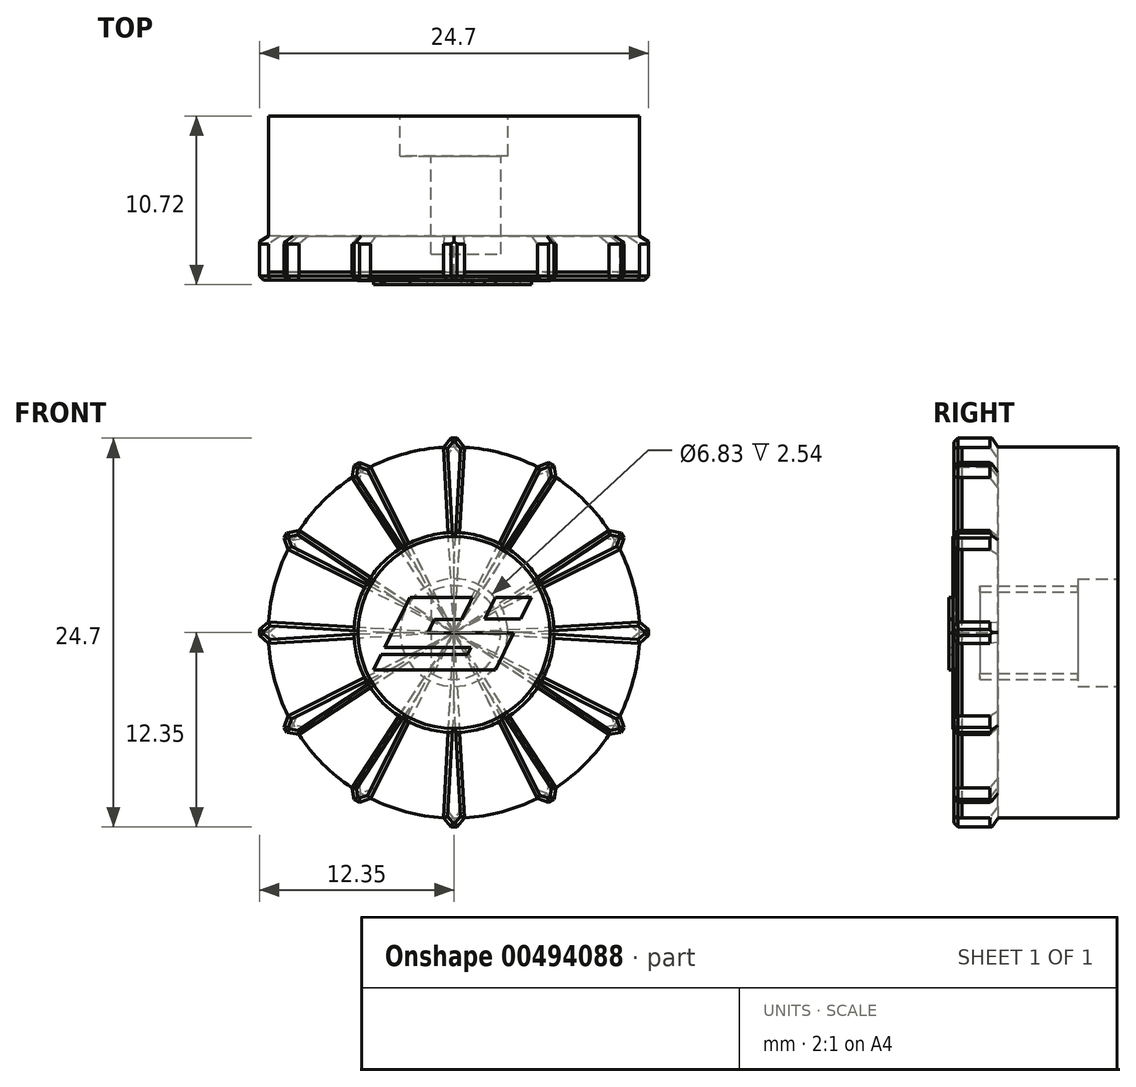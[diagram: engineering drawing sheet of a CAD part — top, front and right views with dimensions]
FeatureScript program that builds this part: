
annotation { "Feature Type Name" : "Feature", "Feature Type Description" : "" }
export const myFeature = defineFeature(function(context is Context, id is Id, definition is map)
    precondition{}
    {
        {
            var Q0;
            Q0=qCreatedBy(makeId("Front.planeOp"),FACE);
            var sketch = newSketch(context, id + "F0", { "sketchPlane" : qUnion([Q0])});
            skCircle(sketch, "E0", {"center": v(-36.3, 18.86) * mm, "radius": 11.79 * mm});
            skSolve(sketch);
        }
        {
            var Q0;
            Q0=makeQuery(id+"F0.imprint","IMPRINT",FACE,{"disambiguationData":[TD([[makeQuery(id+"F0.imprint","IMPRINT",EDGE,{"derivedFrom":sQuery(id+"F0.wireOp",EDGE,"E0")}),1.0]])]});
            extrude(context, id + "F1", {"entities" : qUnion([Q0]), "depth" : 9.9 * mm});
        }
        {
            var Q0;
            Q0=makeQuery(id+"F1.opExtrude","CAP_FACE",FACE,{"disambiguationData":[OSD([sQuery(id+"F0.wireOp",EDGE,"E0")])],"isStart":true});
            var sketch = newSketch(context, id + "F2", { "sketchPlane" : qUnion([Q0])});
            skArc(sketch, "E1", {"start": v(37.76, 21.44) * mm, "mid": v(33.32, 18.86) * mm, "end": v(37.76, 16.28) * mm});
            skLineSegment(sketch, "E2", {"start": v(37.76, 21.44) * mm, "end": v(37.76, 16.28) * mm});
            skSolve(sketch);
        }
        {
            var Q0;
            Q0=makeQuery(id+"F2.imprint","IMPRINT",FACE,{"disambiguationData":[TD([[makeQuery(id+"F2.imprint","IMPRINT",EDGE,{"derivedFrom":sQuery(id+"F2.wireOp",EDGE,"E1")}),1.0]])]});
            extrude(context, id + "F3", {"entities" : qUnion([Q0]), "operationType" : NewBodyOperationType.REMOVE, "oppositeDirection" : true, "depth" : 8.76 * mm});
        }
        {
            var Q0;
            Q0=makeQuery(id+"F1.opExtrude","CAP_FACE",FACE,{"disambiguationData":[OSD([sQuery(id+"F0.wireOp",EDGE,"E0")])],"isStart":true});
            var sketch = newSketch(context, id + "F4", { "sketchPlane" : qUnion([Q0])});
            skCircle(sketch, "E3", {"center": v(36.3, 18.86) * mm, "radius": 3.42 * mm});
            skSolve(sketch);
        }
        {
            var Q0;
            Q0=makeQuery(id+"F4.imprint","IMPRINT",FACE,{"disambiguationData":[TD([[makeQuery(id+"F4.imprint","IMPRINT",EDGE,{"derivedFrom":sQuery(id+"F4.wireOp",EDGE,"E3")}),1.0]])]});
            var Q1;
            Q1=sQuery(id+"F4.wireOp",EDGE,"E3");
            extrude(context, id + "F5", {"entities" : qUnion([Q0]), "operationType" : NewBodyOperationType.REMOVE, "surfaceEntities" : qUnion([Q1]), "oppositeDirection" : true, "depth" : 2.54 * mm});
        }
        {
            var Q0;
            Q0=qCreatedBy(makeId("Front.planeOp"),FACE);
            var sketch = newSketch(context, id + "F6", { "sketchPlane" : qUnion([Q0])});
            skLineSegment(sketch, "E4", {"start": v(-36.97, 30.63) * mm, "end": v(-36.48, 31.2) * mm});
            skLineSegment(sketch, "E5", {"start": v(-36.48, 31.2) * mm, "end": v(-36.1, 31.2) * mm});
            skLineSegment(sketch, "E6", {"start": v(-36.1, 31.2) * mm, "end": v(-35.6, 30.63) * mm});
            skLineSegment(sketch, "E7", {"start": v(-36.3, 18.86) * mm, "end": v(-36.97, 30.63) * mm});
            skLineSegment(sketch, "E8", {"start": v(-35.6, 30.63) * mm, "end": v(-36.3, 18.86) * mm});
            skLineSegment(sketch, "E9.1.0", {"start": v(-41.58, 29.39) * mm, "end": v(-36.3, 18.86) * mm});
            skLineSegment(sketch, "E9.1.1", {"start": v(-36.3, 18.86) * mm, "end": v(-42.76, 28.7) * mm});
            skLineSegment(sketch, "E9.1.2", {"start": v(-42.76, 28.7) * mm, "end": v(-42.63, 29.46) * mm});
            skLineSegment(sketch, "E9.1.3", {"start": v(-42.63, 29.46) * mm, "end": v(-42.3, 29.65) * mm});
            skLineSegment(sketch, "E9.1.4", {"start": v(-42.3, 29.65) * mm, "end": v(-41.58, 29.39) * mm});
            skLineSegment(sketch, "E9.2.0", {"start": v(-46.14, 25.33) * mm, "end": v(-36.3, 18.86) * mm});
            skLineSegment(sketch, "E9.2.1", {"start": v(-36.3, 18.86) * mm, "end": v(-46.82, 24.15) * mm});
            skLineSegment(sketch, "E9.2.2", {"start": v(-46.82, 24.15) * mm, "end": v(-47.08, 24.87) * mm});
            skLineSegment(sketch, "E9.2.3", {"start": v(-47.08, 24.87) * mm, "end": v(-46.9, 25.2) * mm});
            skLineSegment(sketch, "E9.2.4", {"start": v(-46.9, 25.2) * mm, "end": v(-46.14, 25.33) * mm});
            skLineSegment(sketch, "E9.3.0", {"start": v(-48.06, 19.54) * mm, "end": v(-36.3, 18.86) * mm});
            skLineSegment(sketch, "E9.3.1", {"start": v(-36.3, 18.86) * mm, "end": v(-48.06, 18.18) * mm});
            skLineSegment(sketch, "E9.3.2", {"start": v(-48.06, 18.18) * mm, "end": v(-48.64, 18.67) * mm});
            skLineSegment(sketch, "E9.3.3", {"start": v(-48.64, 18.67) * mm, "end": v(-48.64, 19.05) * mm});
            skLineSegment(sketch, "E9.3.4", {"start": v(-48.64, 19.05) * mm, "end": v(-48.06, 19.54) * mm});
            skLineSegment(sketch, "E9.4.0", {"start": v(-46.82, 13.57) * mm, "end": v(-36.3, 18.86) * mm});
            skLineSegment(sketch, "E9.4.1", {"start": v(-36.3, 18.86) * mm, "end": v(-46.14, 12.39) * mm});
            skLineSegment(sketch, "E9.4.2", {"start": v(-46.14, 12.39) * mm, "end": v(-46.9, 12.52) * mm});
            skLineSegment(sketch, "E9.4.3", {"start": v(-46.9, 12.52) * mm, "end": v(-47.08, 12.85) * mm});
            skLineSegment(sketch, "E9.4.4", {"start": v(-47.08, 12.85) * mm, "end": v(-46.82, 13.57) * mm});
            skLineSegment(sketch, "E9.5.0", {"start": v(-42.76, 9.01) * mm, "end": v(-36.3, 18.86) * mm});
            skLineSegment(sketch, "E9.5.1", {"start": v(-36.3, 18.86) * mm, "end": v(-41.58, 8.33) * mm});
            skLineSegment(sketch, "E9.5.2", {"start": v(-41.58, 8.33) * mm, "end": v(-42.3, 8.07) * mm});
            skLineSegment(sketch, "E9.5.3", {"start": v(-42.3, 8.07) * mm, "end": v(-42.63, 8.26) * mm});
            skLineSegment(sketch, "E9.5.4", {"start": v(-42.63, 8.26) * mm, "end": v(-42.76, 9.01) * mm});
            skLineSegment(sketch, "E9.6.0", {"start": v(-36.97, 7.1) * mm, "end": v(-36.3, 18.86) * mm});
            skLineSegment(sketch, "E9.6.1", {"start": v(-36.3, 18.86) * mm, "end": v(-35.6, 7.1) * mm});
            skLineSegment(sketch, "E9.6.2", {"start": v(-35.6, 7.1) * mm, "end": v(-36.1, 6.5) * mm});
            skLineSegment(sketch, "E9.6.3", {"start": v(-36.1, 6.5) * mm, "end": v(-36.48, 6.5) * mm});
            skLineSegment(sketch, "E9.6.4", {"start": v(-36.48, 6.5) * mm, "end": v(-36.97, 7.1) * mm});
            skLineSegment(sketch, "E9.7.0", {"start": v(-31, 8.33) * mm, "end": v(-36.3, 18.86) * mm});
            skLineSegment(sketch, "E9.7.1", {"start": v(-36.3, 18.86) * mm, "end": v(-29.82, 9.01) * mm});
            skLineSegment(sketch, "E9.7.2", {"start": v(-29.82, 9.01) * mm, "end": v(-29.95, 8.26) * mm});
            skLineSegment(sketch, "E9.7.3", {"start": v(-29.95, 8.26) * mm, "end": v(-30.28, 8.07) * mm});
            skLineSegment(sketch, "E9.7.4", {"start": v(-30.28, 8.07) * mm, "end": v(-31, 8.33) * mm});
            skLineSegment(sketch, "E9.8.0", {"start": v(-26.44, 12.39) * mm, "end": v(-36.3, 18.86) * mm});
            skLineSegment(sketch, "E9.8.1", {"start": v(-36.3, 18.86) * mm, "end": v(-25.76, 13.57) * mm});
            skLineSegment(sketch, "E9.8.2", {"start": v(-25.76, 13.57) * mm, "end": v(-25.5, 12.85) * mm});
            skLineSegment(sketch, "E9.8.3", {"start": v(-25.5, 12.85) * mm, "end": v(-25.7, 12.52) * mm});
            skLineSegment(sketch, "E9.8.4", {"start": v(-25.7, 12.52) * mm, "end": v(-26.44, 12.39) * mm});
            skLineSegment(sketch, "E9.9.0", {"start": v(-24.52, 18.18) * mm, "end": v(-36.3, 18.86) * mm});
            skLineSegment(sketch, "E9.9.1", {"start": v(-36.3, 18.86) * mm, "end": v(-24.52, 19.54) * mm});
            skLineSegment(sketch, "E9.9.2", {"start": v(-24.52, 19.54) * mm, "end": v(-23.94, 19.05) * mm});
            skLineSegment(sketch, "E9.9.3", {"start": v(-23.94, 19.05) * mm, "end": v(-23.94, 18.67) * mm});
            skLineSegment(sketch, "E9.9.4", {"start": v(-23.94, 18.67) * mm, "end": v(-24.52, 18.18) * mm});
            skLineSegment(sketch, "E9.10.0", {"start": v(-25.76, 24.15) * mm, "end": v(-36.3, 18.86) * mm});
            skLineSegment(sketch, "E9.10.1", {"start": v(-36.3, 18.86) * mm, "end": v(-26.44, 25.33) * mm});
            skLineSegment(sketch, "E9.10.2", {"start": v(-26.44, 25.33) * mm, "end": v(-25.7, 25.2) * mm});
            skLineSegment(sketch, "E9.10.3", {"start": v(-25.7, 25.2) * mm, "end": v(-25.5, 24.87) * mm});
            skLineSegment(sketch, "E9.10.4", {"start": v(-25.5, 24.87) * mm, "end": v(-25.76, 24.15) * mm});
            skLineSegment(sketch, "E9.11.0", {"start": v(-29.82, 28.7) * mm, "end": v(-36.3, 18.86) * mm});
            skLineSegment(sketch, "E9.11.1", {"start": v(-36.3, 18.86) * mm, "end": v(-31, 29.39) * mm});
            skLineSegment(sketch, "E9.11.2", {"start": v(-31, 29.39) * mm, "end": v(-30.28, 29.65) * mm});
            skLineSegment(sketch, "E9.11.3", {"start": v(-30.28, 29.65) * mm, "end": v(-29.95, 29.46) * mm});
            skLineSegment(sketch, "E9.11.4", {"start": v(-29.95, 29.46) * mm, "end": v(-29.82, 28.7) * mm});
            skPoint(sketch, "E9.center", {"position": v(-36.3, 18.86) * mm});
            skSolve(sketch);
        }
        {
            var Q0;
            Q0=makeQuery(id+"F6.imprint","IMPRINT",FACE,{"disambiguationData":[TD([[makeQuery(id+"F6.imprint","IMPRINT",EDGE,{"derivedFrom":sQuery(id+"F6.wireOp",EDGE,"E9.8.0")}),-1.0]])]});
            var Q1;
            Q1=makeQuery(id+"F6.imprint","IMPRINT",FACE,{"disambiguationData":[TD([[makeQuery(id+"F6.imprint","IMPRINT",EDGE,{"derivedFrom":sQuery(id+"F6.wireOp",EDGE,"E9.9.0")}),-1.0]])]});
            var Q2;
            Q2=makeQuery(id+"F6.imprint","IMPRINT",FACE,{"disambiguationData":[TD([[makeQuery(id+"F6.imprint","IMPRINT",EDGE,{"derivedFrom":sQuery(id+"F6.wireOp",EDGE,"E9.10.0")}),-1.0]])]});
            var Q3;
            Q3=makeQuery(id+"F6.imprint","IMPRINT",FACE,{"disambiguationData":[TD([[makeQuery(id+"F6.imprint","IMPRINT",EDGE,{"derivedFrom":sQuery(id+"F6.wireOp",EDGE,"E9.11.0")}),-1.0]])]});
            var Q4;
            Q4=makeQuery(id+"F6.imprint","IMPRINT",FACE,{"disambiguationData":[TD([[makeQuery(id+"F6.imprint","IMPRINT",EDGE,{"derivedFrom":sQuery(id+"F6.wireOp",EDGE,"E4")}),-1.0]])]});
            var Q5;
            Q5=makeQuery(id+"F6.imprint","IMPRINT",FACE,{"disambiguationData":[TD([[makeQuery(id+"F6.imprint","IMPRINT",EDGE,{"derivedFrom":sQuery(id+"F6.wireOp",EDGE,"E9.2.0")}),-1.0]])]});
            var Q6;
            Q6=makeQuery(id+"F6.imprint","IMPRINT",FACE,{"disambiguationData":[TD([[makeQuery(id+"F6.imprint","IMPRINT",EDGE,{"derivedFrom":sQuery(id+"F6.wireOp",EDGE,"E9.3.0")}),-1.0]])]});
            var Q7;
            Q7=makeQuery(id+"F6.imprint","IMPRINT",FACE,{"disambiguationData":[TD([[makeQuery(id+"F6.imprint","IMPRINT",EDGE,{"derivedFrom":sQuery(id+"F6.wireOp",EDGE,"E9.4.0")}),-1.0]])]});
            var Q8;
            Q8=makeQuery(id+"F6.imprint","IMPRINT",FACE,{"disambiguationData":[TD([[makeQuery(id+"F6.imprint","IMPRINT",EDGE,{"derivedFrom":sQuery(id+"F6.wireOp",EDGE,"E9.5.0")}),-1.0]])]});
            var Q9;
            Q9=makeQuery(id+"F6.imprint","IMPRINT",FACE,{"disambiguationData":[TD([[makeQuery(id+"F6.imprint","IMPRINT",EDGE,{"derivedFrom":sQuery(id+"F6.wireOp",EDGE,"E9.6.0")}),-1.0]])]});
            var Q10;
            Q10=makeQuery(id+"F6.imprint","IMPRINT",FACE,{"disambiguationData":[TD([[makeQuery(id+"F6.imprint","IMPRINT",EDGE,{"derivedFrom":sQuery(id+"F6.wireOp",EDGE,"E9.7.0")}),-1.0]])]});
            var Q11;
            Q11=makeQuery(id+"F6.imprint","IMPRINT",FACE,{"disambiguationData":[TD([[makeQuery(id+"F6.imprint","IMPRINT",EDGE,{"derivedFrom":sQuery(id+"F6.wireOp",EDGE,"E9.1.0")}),-1.0]])]});
            var Q12;
            Q12=sQuery(id+"F6.wireOp",EDGE,"E4");
            var Q13;
            Q13=sQuery(id+"F6.wireOp",EDGE,"E5");
            var Q14;
            Q14=sQuery(id+"F6.wireOp",EDGE,"E6");
            var Q15;
            Q15=sQuery(id+"F6.wireOp",EDGE,"E8");
            extrude(context, id + "F7", {"entities" : qUnion([Q0, Q1, Q2, Q3, Q4, Q5, Q6, Q7, Q8, Q9, Q10, Q11]), "surfaceEntities" : qUnion([Q12, Q13, Q14, Q15]), "depth" : 10.4 * mm, "hasSecondDirection" : true, "secondDirectionOppositeDirection" : false, "secondDirectionDepth" : 7.62 * mm});
        }
        {
            var Q0;
            Q0=makeQuery(id+"F7.opExtrude","CAP_EDGE",EDGE,{"disambiguationData":[OSD([sQuery(id+"F6.wireOp",EDGE,"E9.10.3")])],"isStart":true});
            var Q1;
            Q1=makeQuery(id+"F7.opExtrude","CAP_EDGE",EDGE,{"disambiguationData":[OSD([sQuery(id+"F6.wireOp",EDGE,"E9.10.2")])],"isStart":true});
            var Q2;
            Q2=makeQuery(id+"F7.opExtrude","CAP_EDGE",EDGE,{"disambiguationData":[OSD([sQuery(id+"F6.wireOp",EDGE,"E9.10.4")])],"isStart":true});
            var Q3;
            Q3=makeQuery(id+"F7.opExtrude","CAP_EDGE",EDGE,{"disambiguationData":[OSD([sQuery(id+"F6.wireOp",EDGE,"E9.11.3")])],"isStart":true});
            var Q4;
            Q4=makeQuery(id+"F7.opExtrude","CAP_EDGE",EDGE,{"disambiguationData":[OSD([sQuery(id+"F6.wireOp",EDGE,"E9.11.2")])],"isStart":true});
            var Q5;
            Q5=makeQuery(id+"F7.opExtrude","CAP_EDGE",EDGE,{"disambiguationData":[OSD([sQuery(id+"F6.wireOp",EDGE,"E9.11.4")])],"isStart":true});
            var Q6;
            Q6=makeQuery(id+"F7.opExtrude","CAP_EDGE",EDGE,{"disambiguationData":[OSD([sQuery(id+"F6.wireOp",EDGE,"E9.9.2")])],"isStart":true});
            var Q7;
            Q7=makeQuery(id+"F7.opExtrude","CAP_EDGE",EDGE,{"disambiguationData":[OSD([sQuery(id+"F6.wireOp",EDGE,"E9.9.3")])],"isStart":true});
            var Q8;
            Q8=makeQuery(id+"F7.opExtrude","CAP_EDGE",EDGE,{"disambiguationData":[OSD([sQuery(id+"F6.wireOp",EDGE,"E9.9.4")])],"isStart":true});
            var Q9;
            Q9=makeQuery(id+"F7.opExtrude","CAP_EDGE",EDGE,{"disambiguationData":[OSD([sQuery(id+"F6.wireOp",EDGE,"E9.8.2")])],"isStart":true});
            var Q10;
            Q10=makeQuery(id+"F7.opExtrude","CAP_EDGE",EDGE,{"disambiguationData":[OSD([sQuery(id+"F6.wireOp",EDGE,"E9.8.3")])],"isStart":true});
            var Q11;
            Q11=makeQuery(id+"F7.opExtrude","CAP_EDGE",EDGE,{"disambiguationData":[OSD([sQuery(id+"F6.wireOp",EDGE,"E9.8.4")])],"isStart":true});
            var Q12;
            Q12=makeQuery(id+"F7.opExtrude","CAP_EDGE",EDGE,{"disambiguationData":[OSD([sQuery(id+"F6.wireOp",EDGE,"E9.7.2")])],"isStart":true});
            var Q13;
            Q13=makeQuery(id+"F7.opExtrude","CAP_EDGE",EDGE,{"disambiguationData":[OSD([sQuery(id+"F6.wireOp",EDGE,"E9.7.3")])],"isStart":true});
            var Q14;
            Q14=makeQuery(id+"F7.opExtrude","CAP_EDGE",EDGE,{"disambiguationData":[OSD([sQuery(id+"F6.wireOp",EDGE,"E9.7.4")])],"isStart":true});
            var Q15;
            Q15=makeQuery(id+"F7.opExtrude","CAP_EDGE",EDGE,{"disambiguationData":[OSD([sQuery(id+"F6.wireOp",EDGE,"E9.6.3")])],"isStart":true});
            var Q16;
            Q16=makeQuery(id+"F7.opExtrude","CAP_EDGE",EDGE,{"disambiguationData":[OSD([sQuery(id+"F6.wireOp",EDGE,"E9.6.4")])],"isStart":true});
            var Q17;
            Q17=makeQuery(id+"F7.opExtrude","CAP_EDGE",EDGE,{"disambiguationData":[OSD([sQuery(id+"F6.wireOp",EDGE,"E9.6.2")])],"isStart":true});
            var Q18;
            Q18=makeQuery(id+"F7.opExtrude","CAP_EDGE",EDGE,{"disambiguationData":[OSD([sQuery(id+"F6.wireOp",EDGE,"E9.5.2")])],"isStart":true});
            var Q19;
            Q19=makeQuery(id+"F7.opExtrude","CAP_EDGE",EDGE,{"disambiguationData":[OSD([sQuery(id+"F6.wireOp",EDGE,"E9.5.3")])],"isStart":true});
            var Q20;
            Q20=makeQuery(id+"F7.opExtrude","CAP_EDGE",EDGE,{"disambiguationData":[OSD([sQuery(id+"F6.wireOp",EDGE,"E9.5.4")])],"isStart":true});
            var Q21;
            Q21=makeQuery(id+"F7.opExtrude","CAP_EDGE",EDGE,{"disambiguationData":[OSD([sQuery(id+"F6.wireOp",EDGE,"E9.4.2")])],"isStart":true});
            var Q22;
            Q22=makeQuery(id+"F7.opExtrude","CAP_EDGE",EDGE,{"disambiguationData":[OSD([sQuery(id+"F6.wireOp",EDGE,"E9.4.3")])],"isStart":true});
            var Q23;
            Q23=makeQuery(id+"F7.opExtrude","CAP_EDGE",EDGE,{"disambiguationData":[OSD([sQuery(id+"F6.wireOp",EDGE,"E9.4.4")])],"isStart":true});
            var Q24;
            Q24=makeQuery(id+"F7.opExtrude","CAP_EDGE",EDGE,{"disambiguationData":[OSD([sQuery(id+"F6.wireOp",EDGE,"E9.3.3")])],"isStart":true});
            var Q25;
            Q25=makeQuery(id+"F7.opExtrude","CAP_EDGE",EDGE,{"disambiguationData":[OSD([sQuery(id+"F6.wireOp",EDGE,"E9.3.4")])],"isStart":true});
            var Q26;
            Q26=makeQuery(id+"F7.opExtrude","CAP_EDGE",EDGE,{"disambiguationData":[OSD([sQuery(id+"F6.wireOp",EDGE,"E9.3.2")])],"isStart":true});
            var Q27;
            Q27=makeQuery(id+"F7.opExtrude","CAP_EDGE",EDGE,{"disambiguationData":[OSD([sQuery(id+"F6.wireOp",EDGE,"E9.2.4")])],"isStart":true});
            var Q28;
            Q28=makeQuery(id+"F7.opExtrude","CAP_EDGE",EDGE,{"disambiguationData":[OSD([sQuery(id+"F6.wireOp",EDGE,"E9.2.3")])],"isStart":true});
            var Q29;
            Q29=makeQuery(id+"F7.opExtrude","CAP_EDGE",EDGE,{"disambiguationData":[OSD([sQuery(id+"F6.wireOp",EDGE,"E9.2.2")])],"isStart":true});
            var Q30;
            Q30=makeQuery(id+"F7.opExtrude","CAP_EDGE",EDGE,{"disambiguationData":[OSD([sQuery(id+"F6.wireOp",EDGE,"E9.1.3")])],"isStart":true});
            var Q31;
            Q31=makeQuery(id+"F7.opExtrude","CAP_EDGE",EDGE,{"disambiguationData":[OSD([sQuery(id+"F6.wireOp",EDGE,"E9.1.2")])],"isStart":true});
            var Q32;
            Q32=makeQuery(id+"F7.opExtrude","CAP_EDGE",EDGE,{"disambiguationData":[OSD([sQuery(id+"F6.wireOp",EDGE,"E9.1.4")])],"isStart":true});
            var Q33;
            Q33=makeQuery(id+"F7.opExtrude","CAP_EDGE",EDGE,{"disambiguationData":[OSD([sQuery(id+"F6.wireOp",EDGE,"E6")])],"isStart":true});
            var Q34;
            Q34=makeQuery(id+"F7.opExtrude","CAP_EDGE",EDGE,{"disambiguationData":[OSD([sQuery(id+"F6.wireOp",EDGE,"E5")])],"isStart":true});
            var Q35;
            Q35=makeQuery(id+"F7.opExtrude","CAP_EDGE",EDGE,{"disambiguationData":[OSD([sQuery(id+"F6.wireOp",EDGE,"E4")])],"isStart":true});
            chamfer(context, id + "F8", {"entities" : qUnion([Q0, Q1, Q2, Q3, Q4, Q5, Q6, Q7, Q8, Q9, Q10, Q11, Q12, Q13, Q14, Q15, Q16, Q17, Q18, Q19, Q20, Q21, Q22, Q23, Q24, Q25, Q26, Q27, Q28, Q29, Q30, Q31, Q32, Q33, Q34, Q35]), "chamferType" : ChamferType.OFFSET_ANGLE, "width" : 0.5 * mm, "oppositeDirection" : false, "angle" : 45 * degree, "tangentPropagation" : true});
        }
        {
            var Q0;
            Q0=makeQuery(id+"F7.opExtrude","CAP_FACE",FACE,{"disambiguationData":[OSD([sQuery(id+"F6.wireOp",EDGE,"E9.11.0"),sQuery(id+"F6.wireOp",EDGE,"E9.11.1"),sQuery(id+"F6.wireOp",EDGE,"E9.11.2"),sQuery(id+"F6.wireOp",EDGE,"E9.11.3"),sQuery(id+"F6.wireOp",EDGE,"E9.11.4")])],"isStart":false});
            var Q1;
            Q1=makeQuery(id+"F7.opExtrude","CAP_FACE",FACE,{"disambiguationData":[OSD([sQuery(id+"F6.wireOp",EDGE,"E9.10.0"),sQuery(id+"F6.wireOp",EDGE,"E9.10.1"),sQuery(id+"F6.wireOp",EDGE,"E9.10.2"),sQuery(id+"F6.wireOp",EDGE,"E9.10.3"),sQuery(id+"F6.wireOp",EDGE,"E9.10.4")])],"isStart":false});
            var Q2;
            Q2=makeQuery(id+"F7.opExtrude","CAP_FACE",FACE,{"disambiguationData":[OSD([sQuery(id+"F6.wireOp",EDGE,"E9.9.0"),sQuery(id+"F6.wireOp",EDGE,"E9.9.1"),sQuery(id+"F6.wireOp",EDGE,"E9.9.2"),sQuery(id+"F6.wireOp",EDGE,"E9.9.3"),sQuery(id+"F6.wireOp",EDGE,"E9.9.4")])],"isStart":false});
            var Q3;
            Q3=makeQuery(id+"F7.opExtrude","CAP_FACE",FACE,{"disambiguationData":[OSD([sQuery(id+"F6.wireOp",EDGE,"E9.8.0"),sQuery(id+"F6.wireOp",EDGE,"E9.8.1"),sQuery(id+"F6.wireOp",EDGE,"E9.8.2"),sQuery(id+"F6.wireOp",EDGE,"E9.8.3"),sQuery(id+"F6.wireOp",EDGE,"E9.8.4")])],"isStart":false});
            var Q4;
            Q4=makeQuery(id+"F7.opExtrude","CAP_FACE",FACE,{"disambiguationData":[OSD([sQuery(id+"F6.wireOp",EDGE,"E9.7.0"),sQuery(id+"F6.wireOp",EDGE,"E9.7.1"),sQuery(id+"F6.wireOp",EDGE,"E9.7.2"),sQuery(id+"F6.wireOp",EDGE,"E9.7.3"),sQuery(id+"F6.wireOp",EDGE,"E9.7.4")])],"isStart":false});
            var Q5;
            Q5=makeQuery(id+"F7.opExtrude","CAP_FACE",FACE,{"disambiguationData":[OSD([sQuery(id+"F6.wireOp",EDGE,"E9.6.0"),sQuery(id+"F6.wireOp",EDGE,"E9.6.1"),sQuery(id+"F6.wireOp",EDGE,"E9.6.2"),sQuery(id+"F6.wireOp",EDGE,"E9.6.3"),sQuery(id+"F6.wireOp",EDGE,"E9.6.4")])],"isStart":false});
            var Q6;
            Q6=makeQuery(id+"F7.opExtrude","CAP_FACE",FACE,{"disambiguationData":[OSD([sQuery(id+"F6.wireOp",EDGE,"E9.5.0"),sQuery(id+"F6.wireOp",EDGE,"E9.5.1"),sQuery(id+"F6.wireOp",EDGE,"E9.5.2"),sQuery(id+"F6.wireOp",EDGE,"E9.5.3"),sQuery(id+"F6.wireOp",EDGE,"E9.5.4")])],"isStart":false});
            var Q7;
            Q7=makeQuery(id+"F7.opExtrude","CAP_FACE",FACE,{"disambiguationData":[OSD([sQuery(id+"F6.wireOp",EDGE,"E9.4.0"),sQuery(id+"F6.wireOp",EDGE,"E9.4.1"),sQuery(id+"F6.wireOp",EDGE,"E9.4.2"),sQuery(id+"F6.wireOp",EDGE,"E9.4.3"),sQuery(id+"F6.wireOp",EDGE,"E9.4.4")])],"isStart":false});
            var Q8;
            Q8=makeQuery(id+"F7.opExtrude","CAP_FACE",FACE,{"disambiguationData":[OSD([sQuery(id+"F6.wireOp",EDGE,"E9.3.0"),sQuery(id+"F6.wireOp",EDGE,"E9.3.1"),sQuery(id+"F6.wireOp",EDGE,"E9.3.2"),sQuery(id+"F6.wireOp",EDGE,"E9.3.3"),sQuery(id+"F6.wireOp",EDGE,"E9.3.4")])],"isStart":false});
            var Q9;
            Q9=makeQuery(id+"F7.opExtrude","CAP_FACE",FACE,{"disambiguationData":[OSD([sQuery(id+"F6.wireOp",EDGE,"E9.2.0"),sQuery(id+"F6.wireOp",EDGE,"E9.2.1"),sQuery(id+"F6.wireOp",EDGE,"E9.2.2"),sQuery(id+"F6.wireOp",EDGE,"E9.2.3"),sQuery(id+"F6.wireOp",EDGE,"E9.2.4")])],"isStart":false});
            var Q10;
            Q10=makeQuery(id+"F7.opExtrude","CAP_FACE",FACE,{"disambiguationData":[OSD([sQuery(id+"F6.wireOp",EDGE,"E9.1.0"),sQuery(id+"F6.wireOp",EDGE,"E9.1.1"),sQuery(id+"F6.wireOp",EDGE,"E9.1.2"),sQuery(id+"F6.wireOp",EDGE,"E9.1.3"),sQuery(id+"F6.wireOp",EDGE,"E9.1.4")])],"isStart":false});
            var Q11;
            Q11=makeQuery(id+"F7.opExtrude","CAP_FACE",FACE,{"disambiguationData":[OSD([sQuery(id+"F6.wireOp",EDGE,"E4"),sQuery(id+"F6.wireOp",EDGE,"E5"),sQuery(id+"F6.wireOp",EDGE,"E6"),sQuery(id+"F6.wireOp",EDGE,"E7"),sQuery(id+"F6.wireOp",EDGE,"E8")])],"isStart":false});
            chamfer(context, id + "F9", {"entities" : qUnion([Q0, Q1, Q2, Q3, Q4, Q5, Q6, Q7, Q8, Q9, Q10, Q11]), "chamferType" : ChamferType.OFFSET_ANGLE, "width" : 0.25 * mm, "oppositeDirection" : false, "angle" : 45 * degree, "tangentPropagation" : true});
        }
        {
            var Q0;
            Q0=makeQuery(id+"F1.opExtrude","CAP_FACE",FACE,{"disambiguationData":[OSD([sQuery(id+"F0.wireOp",EDGE,"E0")])],"isStart":false});
            var sketch = newSketch(context, id + "F10", { "sketchPlane" : qUnion([Q0])});
            skCircle(sketch, "E10", {"center": v(-36.3, 18.86) * mm, "radius": 6.35 * mm});
            skSolve(sketch);
        }
        {
            var Q0;
            Q0=makeQuery(id+"F10.imprint","IMPRINT",FACE,{"disambiguationData":[TD([[makeQuery(id+"F10.imprint","IMPRINT",EDGE,{"derivedFrom":sQuery(id+"F10.wireOp",EDGE,"E10")}),1.0]])]});
            extrude(context, id + "F11", {"entities" : qUnion([Q0]), "depth" : 0.56 * mm});
        }
        {
            var Q0;
            Q0=makeQuery(id+"F11.opExtrude","CAP_FACE",FACE,{"disambiguationData":[OSD([sQuery(id+"F10.wireOp",EDGE,"E10")])],"isStart":false});
            chamfer(context, id + "F12", {"entities" : qUnion([Q0]), "chamferType" : ChamferType.OFFSET_ANGLE, "width" : 0.25 * mm, "oppositeDirection" : false, "angle" : 45 * degree, "tangentPropagation" : true});
        }
        {
            var Q0;
            Q0=makeQuery(id+"F11.opExtrude","CAP_FACE",FACE,{"disambiguationData":[OSD([sQuery(id+"F10.wireOp",EDGE,"E10")])],"isStart":false});
            var sketch = newSketch(context, id + "F13", { "sketchPlane" : qUnion([Q0])});
            skLineSegment(sketch, "E11", {"start": v(-11.2, 7.58) * mm, "end": v(16.33, 7.58) * mm, "construction": true});
            skLineSegment(sketch, "E12", {"start": v(16.33, 7.58) * mm, "end": v(8.13, -8.93) * mm, "construction": true});
            skLineSegment(sketch, "E13", {"start": v(8.13, -8.93) * mm, "end": v(-19.52, -8.93) * mm, "construction": true});
            skLineSegment(sketch, "E14", {"start": v(-19.52, -8.93) * mm, "end": v(-11.2, 7.58) * mm, "construction": true});
            skLineSegment(sketch, "E15", {"start": v(-11.2, 7.58) * mm, "end": v(2.97, 7.58) * mm});
            skLineSegment(sketch, "E16", {"start": v(2.97, 7.58) * mm, "end": v(0.46, 2.6) * mm});
            skLineSegment(sketch, "E17", {"start": v(0.46, 2.6) * mm, "end": v(-5.61, 2.6) * mm});
            skLineSegment(sketch, "E18", {"start": v(-5.61, 2.6) * mm, "end": v(-7.2, -0.56) * mm});
            skLineSegment(sketch, "E19", {"start": v(-7.2, -0.56) * mm, "end": v(12.23, -0.56) * mm});
            skPoint(sketch, "E19.endSnap0", {"position": v(12.23, -0.68) * mm});
            skLineSegment(sketch, "E20", {"start": v(12.23, -0.56) * mm, "end": v(8.13, -8.93) * mm});
            skLineSegment(sketch, "E21", {"start": v(-19.52, -8.93) * mm, "end": v(-17.74, -5.41) * mm});
            skLineSegment(sketch, "E22", {"start": v(-17.74, -5.41) * mm, "end": v(1.84, -5.41) * mm});
            skLineSegment(sketch, "E23", {"start": v(1.84, -5.41) * mm, "end": v(2.63, -3.81) * mm});
            skLineSegment(sketch, "E24", {"start": v(2.63, -3.81) * mm, "end": v(-16.94, -3.81) * mm});
            skLineSegment(sketch, "E25", {"start": v(-16.94, -3.81) * mm, "end": v(-11.2, 7.58) * mm});
            skLineSegment(sketch, "E26", {"start": v(8.13, 7.58) * mm, "end": v(5.68, 2.64) * mm});
            skLineSegment(sketch, "E27", {"start": v(5.68, 2.64) * mm, "end": v(13.87, 2.64) * mm});
            skLineSegment(sketch, "E28", {"start": v(13.87, 2.64) * mm, "end": v(16.33, 7.58) * mm});
            skLineSegment(sketch, "E29", {"start": v(-19.52, -8.93) * mm, "end": v(8.13, -8.93) * mm});
            skLineSegment(sketch, "E30", {"start": v(8.13, 7.58) * mm, "end": v(16.33, 7.58) * mm});
            skCircle(sketch, "E31.0.0", {"center": v(-36.3, 18.86) * mm, "radius": 6.1 * mm});
            skSolve(sketch);
        }
        {
            var Q0;
            Q0=makeQuery(id+"F13.imprint","IMPRINT",FACE,{"disambiguationData":[TD([[makeQuery(id+"F13.imprint","IMPRINT",EDGE,{"derivedFrom":sQuery(id+"F13.wireOp",EDGE,"E26")}),1.0]])]});
            var Q1;
            Q1=makeQuery(id+"F13.imprint","IMPRINT",FACE,{"disambiguationData":[TD([[makeQuery(id+"F13.imprint","IMPRINT",EDGE,{"derivedFrom":sQuery(id+"F13.wireOp",EDGE,"E15")}),-1.0]])]});
            extrude(context, id + "F14", {"entities" : qUnion([Q0, Q1]), "operationType" : NewBodyOperationType.ADD, "depth" : 1.27 * mm});
        }
        {
            var Q0;
            Q0=makeQuery(id+"F14.opExtrude","SWEPT_BODY",BODY,{"disambiguationData":[OSD([sQuery(id+"F13.wireOp",EDGE,"E15"),sQuery(id+"F13.wireOp",EDGE,"E16"),sQuery(id+"F13.wireOp",EDGE,"E17"),sQuery(id+"F13.wireOp",EDGE,"E18"),sQuery(id+"F13.wireOp",EDGE,"E19"),sQuery(id+"F13.wireOp",EDGE,"E20"),sQuery(id+"F13.wireOp",EDGE,"E21"),sQuery(id+"F13.wireOp",EDGE,"E22"),sQuery(id+"F13.wireOp",EDGE,"E23"),sQuery(id+"F13.wireOp",EDGE,"E24"),sQuery(id+"F13.wireOp",EDGE,"E25"),sQuery(id+"F13.wireOp",EDGE,"E29")])]});
            var Q1;
            Q1=makeQuery(id+"F14.opExtrude","SWEPT_BODY",BODY,{"disambiguationData":[OSD([sQuery(id+"F13.wireOp",EDGE,"E26"),sQuery(id+"F13.wireOp",EDGE,"E27"),sQuery(id+"F13.wireOp",EDGE,"E28"),sQuery(id+"F13.wireOp",EDGE,"E30")])]});
            var Q2;
            {var subQ0=sQuery(id+"F10.wireOp",EDGE,"E10");Q2=makeQuery(id+"F12.opChamfer","BLEND_EDGE",EDGE,{"blendedFrom":[makeQuery(id+"F11.opExtrude","CAP_EDGE",EDGE,{"disambiguationData":[OSD([subQ0])],"isStart":false}),makeQuery(id+"F11.opExtrude","CAP_FACE",FACE,{"disambiguationData":[OSD([subQ0])],"isStart":false})],"blendedInto":[makeQuery(id+"F11.opExtrude","CAP_FACE",FACE,{"disambiguationData":[OSD([subQ0])],"isStart":false})]});}
            var Q3;
            Q3=makeQuery(id+"F14.opExtrude","CAP_VERTEX",VERTEX,{"disambiguationData":[OSD([sQuery(id+"F13.wireOp",EDGE,"E18"),sQuery(id+"F13.wireOp",EDGE,"E19")])],"isStart":false});
            transform(context, id + "F15", {"entities" : qUnion([Q0, Q1]), "transformType" : TransformType.SCALE_UNIFORMLY, "scale" : .28, "scalePoint" : qUnion([Q3]), "makeCopy" : false});
        }
        {
            var Q0;
            Q0=makeQuery(id+"F14.opExtrude","SWEPT_BODY",BODY,{"disambiguationData":[OSD([sQuery(id+"F13.wireOp",EDGE,"E15"),sQuery(id+"F13.wireOp",EDGE,"E16"),sQuery(id+"F13.wireOp",EDGE,"E17"),sQuery(id+"F13.wireOp",EDGE,"E18"),sQuery(id+"F13.wireOp",EDGE,"E19"),sQuery(id+"F13.wireOp",EDGE,"E20"),sQuery(id+"F13.wireOp",EDGE,"E21"),sQuery(id+"F13.wireOp",EDGE,"E22"),sQuery(id+"F13.wireOp",EDGE,"E23"),sQuery(id+"F13.wireOp",EDGE,"E24"),sQuery(id+"F13.wireOp",EDGE,"E25"),sQuery(id+"F13.wireOp",EDGE,"E29")])]});
            var Q1;
            Q1=makeQuery(id+"F14.opExtrude","SWEPT_BODY",BODY,{"disambiguationData":[OSD([sQuery(id+"F13.wireOp",EDGE,"E26"),sQuery(id+"F13.wireOp",EDGE,"E27"),sQuery(id+"F13.wireOp",EDGE,"E28"),sQuery(id+"F13.wireOp",EDGE,"E30")])]});
            transform(context, id + "F16", {"entities" : qUnion([Q0, Q1]), "transformType" : TransformType.TRANSLATION_3D, "dx" : -30.76 * mm, "dy" : 0 * mm, "dz" : 19.38 * mm, "makeCopy" : false});
        }
        {
            var Q0;
            Q0=makeQuery(id+"F14.opExtrude","SWEPT_BODY",BODY,{"disambiguationData":[OSD([sQuery(id+"F13.wireOp",EDGE,"E15"),sQuery(id+"F13.wireOp",EDGE,"E16"),sQuery(id+"F13.wireOp",EDGE,"E17"),sQuery(id+"F13.wireOp",EDGE,"E18"),sQuery(id+"F13.wireOp",EDGE,"E19"),sQuery(id+"F13.wireOp",EDGE,"E20"),sQuery(id+"F13.wireOp",EDGE,"E21"),sQuery(id+"F13.wireOp",EDGE,"E22"),sQuery(id+"F13.wireOp",EDGE,"E23"),sQuery(id+"F13.wireOp",EDGE,"E24"),sQuery(id+"F13.wireOp",EDGE,"E25"),sQuery(id+"F13.wireOp",EDGE,"E29")])]});
            var Q1;
            Q1=makeQuery(id+"F14.opExtrude","SWEPT_BODY",BODY,{"disambiguationData":[OSD([sQuery(id+"F13.wireOp",EDGE,"E26"),sQuery(id+"F13.wireOp",EDGE,"E27"),sQuery(id+"F13.wireOp",EDGE,"E28"),sQuery(id+"F13.wireOp",EDGE,"E30")])]});
            transform(context, id + "F17", {"entities" : qUnion([Q0, Q1]), "transformType" : TransformType.TRANSLATION_3D, "dx" : 0 * mm, "dy" : 1.02 * mm, "dz" : 0 * mm, "makeCopy" : false});
        }
    });
